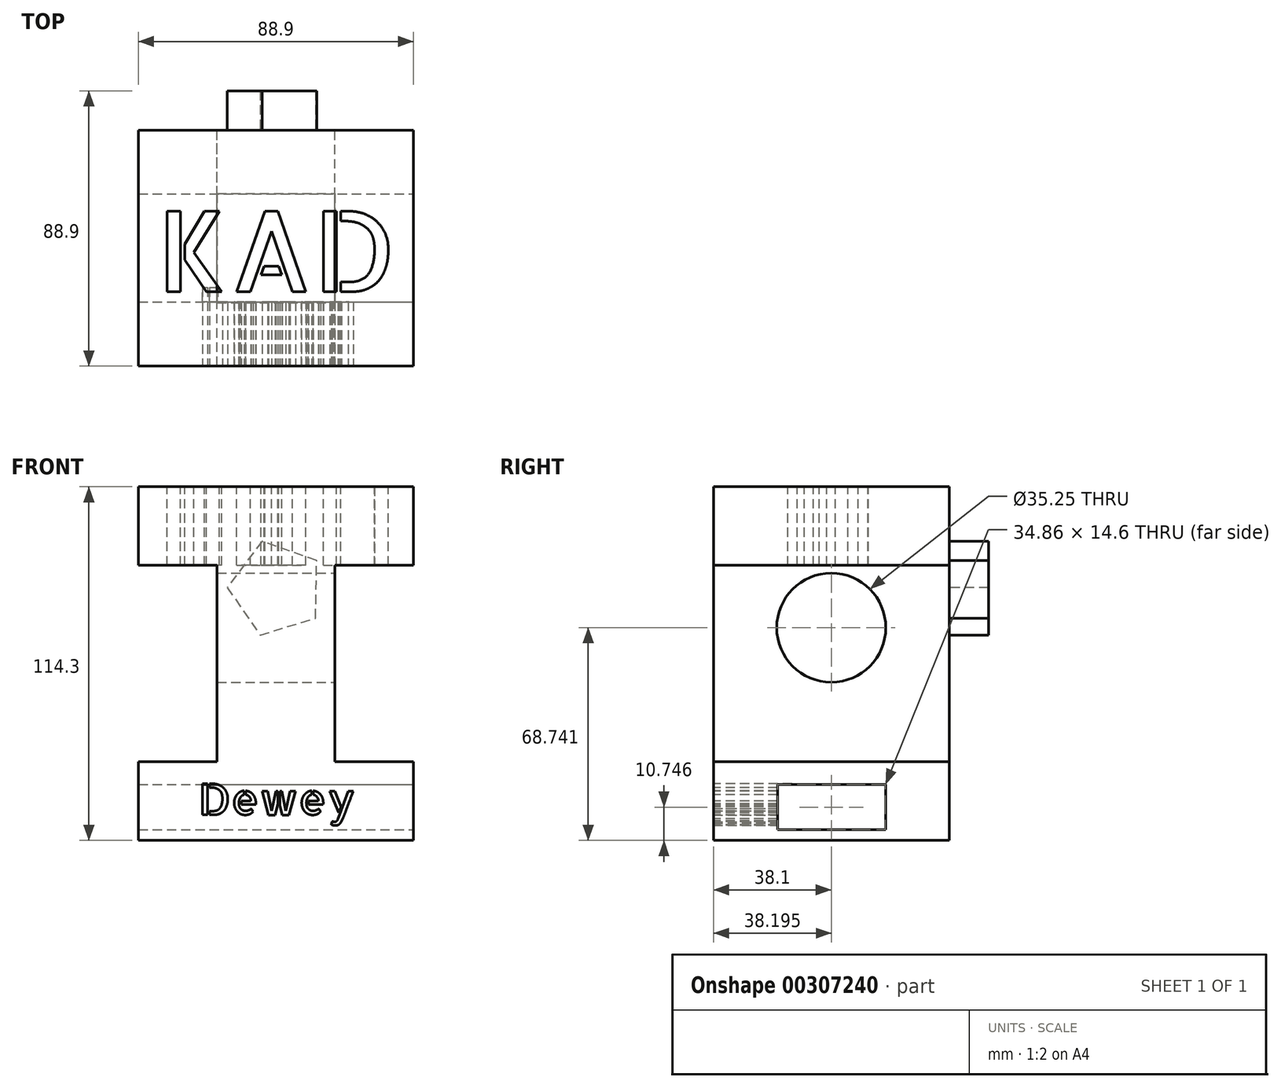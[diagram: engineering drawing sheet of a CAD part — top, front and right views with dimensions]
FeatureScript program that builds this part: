
annotation { "Feature Type Name" : "Feature", "Feature Type Description" : "" }
export const myFeature = defineFeature(function(context is Context, id is Id, definition is map)
    precondition{}
    {
        {
            var Q0;
            Q0=qCreatedBy(makeId("Front.planeOp"),FACE);
            var sketch = newSketch(context, id + "F0", { "sketchPlane" : qUnion([Q0])});
            skLineSegment(sketch, "E0", {"start": v(-31.57, -38.53) * mm, "end": v(57.33, -38.53) * mm});
            skLineSegment(sketch, "E1", {"start": v(57.33, -13.13) * mm, "end": v(57.33, -38.53) * mm});
            skLineSegment(sketch, "E2", {"start": v(57.33, -13.13) * mm, "end": v(31.93, -13.13) * mm});
            skLineSegment(sketch, "E3", {"start": v(31.93, -13.13) * mm, "end": v(31.93, 50.37) * mm});
            skLineSegment(sketch, "E4", {"start": v(31.93, 50.37) * mm, "end": v(57.33, 50.37) * mm});
            skLineSegment(sketch, "E5", {"start": v(57.33, 50.37) * mm, "end": v(57.33, 75.77) * mm});
            skLineSegment(sketch, "E6", {"start": v(57.33, 75.77) * mm, "end": v(-31.57, 75.77) * mm});
            skLineSegment(sketch, "E7", {"start": v(-31.57, 75.77) * mm, "end": v(-31.57, 50.37) * mm});
            skLineSegment(sketch, "E8", {"start": v(-31.57, 50.37) * mm, "end": v(-6.17, 50.37) * mm});
            skLineSegment(sketch, "E9", {"start": v(-6.17, 50.37) * mm, "end": v(-6.17, -13.13) * mm});
            skLineSegment(sketch, "E10", {"start": v(-6.17, -13.13) * mm, "end": v(-31.57, -13.13) * mm});
            skLineSegment(sketch, "E11", {"start": v(-31.57, -13.13) * mm, "end": v(-31.57, -38.53) * mm});
            skSolve(sketch);
        }
        {
            var Q0;
            Q0=makeQuery(id+"F0.imprint","IMPRINT",FACE,{"disambiguationData":[TD([[makeQuery(id+"F0.imprint","IMPRINT",EDGE,{"derivedFrom":sQuery(id+"F0.wireOp",EDGE,"E0")}),1.0]])]});
            extrude(context, id + "F1", {"entities" : qUnion([Q0]), "depth" : 76.2 * mm});
        }
        {
            var Q0;
            Q0=makeQuery(id+"F1.opExtrude","SWEPT_FACE",FACE,{"disambiguationData":[OSD([sQuery(id+"F0.wireOp",EDGE,"E3")])]});
            var sketch = newSketch(context, id + "F2", { "sketchPlane" : qUnion([Q0])});
            skCircle(sketch, "E12", {"center": v(-38.1, 30.21) * mm, "radius": 17.62 * mm});
            skPoint(sketch, "E12.centerSnap0", {"position": v(-38.1, 50.37) * mm});
            skSolve(sketch);
        }
        {
            var Q0;
            Q0=makeQuery(id+"F2.imprint","IMPRINT",FACE,{"disambiguationData":[TD([[makeQuery(id+"F2.imprint","IMPRINT",EDGE,{"derivedFrom":sQuery(id+"F2.wireOp",EDGE,"E12")}),1.0]])]});
            var Q1;
            Q1=sQuery(id+"F2.wireOp",EDGE,"E12");
            extrude(context, id + "F3", {"entities" : qUnion([Q0]), "operationType" : NewBodyOperationType.REMOVE, "surfaceEntities" : qUnion([Q1]), "endBound" : BoundingType.THROUGH_ALL, "oppositeDirection" : true, "depth" : 25.4 * mm});
        }
        {
            var Q0;
            Q0=makeQuery(id+"F1.opExtrude","SWEPT_FACE",FACE,{"disambiguationData":[OSD([sQuery(id+"F0.wireOp",EDGE,"E6")])]});
            var sketch = newSketch(context, id + "F4", { "sketchPlane" : qUnion([Q0])});
            skText(sketch, "E13", { "text": "KAD", "fontName": "AllertaStencil-Regular.ttf"});
            const initialGuessF4  = {"E13": [-0.0256, -0.05217, 1, 0, 0.02604]};
            skSetInitialGuess(sketch, initialGuessF4);
            skSolve(sketch);
        }
        {
            var Q0;
            Q0 = qSketchRegion(id + "F4", true);
            extrude(context, id + "F5", {"entities" : qUnion([Q0]), "operationType" : NewBodyOperationType.REMOVE, "oppositeDirection" : true, "depth" : 25.4 * mm});
        }
        {
            var Q0;
            Q0=makeQuery(id+"F1.opExtrude","SWEPT_FACE",FACE,{"disambiguationData":[OSD([sQuery(id+"F0.wireOp",EDGE,"E1")])]});
            var sketch = newSketch(context, id + "F6", { "sketchPlane" : qUnion([Q0])});
            skLineSegment(sketch, "E14.bottom", {"start": v(-20.57, -20.48) * mm, "end": v(-55.44, -20.48) * mm});
            skLineSegment(sketch, "E14.top", {"start": v(-20.57, -35.08) * mm, "end": v(-55.44, -35.08) * mm});
            skLineSegment(sketch, "E14.left", {"start": v(-20.57, -20.48) * mm, "end": v(-20.57, -35.08) * mm});
            skLineSegment(sketch, "E14.right", {"start": v(-55.44, -20.48) * mm, "end": v(-55.44, -35.08) * mm});
            skSolve(sketch);
        }
        {
            var Q0;
            Q0=makeQuery(id+"F6.imprint","IMPRINT",FACE,{"disambiguationData":[TD([[makeQuery(id+"F6.imprint","IMPRINT",EDGE,{"derivedFrom":sQuery(id+"F6.wireOp",EDGE,"E14.bottom")}),1.0]])]});
            extrude(context, id + "F7", {"entities" : qUnion([Q0]), "operationType" : NewBodyOperationType.REMOVE, "endBound" : BoundingType.THROUGH_ALL, "oppositeDirection" : true, "depth" : 25.4 * mm});
        }
        {
            var Q0;
            Q0=makeQuery(id+"F1.opExtrude","CAP_FACE",FACE,{"disambiguationData":[OSD([sQuery(id+"F0.wireOp",EDGE,"E0"),sQuery(id+"F0.wireOp",EDGE,"E1"),sQuery(id+"F0.wireOp",EDGE,"E2"),sQuery(id+"F0.wireOp",EDGE,"E3"),sQuery(id+"F0.wireOp",EDGE,"E4"),sQuery(id+"F0.wireOp",EDGE,"E5"),sQuery(id+"F0.wireOp",EDGE,"E6"),sQuery(id+"F0.wireOp",EDGE,"E7"),sQuery(id+"F0.wireOp",EDGE,"E8"),sQuery(id+"F0.wireOp",EDGE,"E9"),sQuery(id+"F0.wireOp",EDGE,"E10"),sQuery(id+"F0.wireOp",EDGE,"E11")])],"isStart":true});
            var sketch = newSketch(context, id + "F8", { "sketchPlane" : qUnion([Q0])});
            skCircle(sketch, "E15.cCircle", {"center": v(-13, 42.87) * mm, "radius": 15.9 * mm, "construction": true});
            skLineSegment(sketch, "E15.0", {"start": v(-25.69, 33.27) * mm, "end": v(-26.05, 51.97) * mm});
            skLineSegment(sketch, "E15.1", {"start": v(-26.05, 51.97) * mm, "end": v(-8.37, 58.09) * mm});
            skLineSegment(sketch, "E15.2", {"start": v(-8.37, 58.09) * mm, "end": v(2.9, 43.17) * mm});
            skLineSegment(sketch, "E15.3", {"start": v(2.9, 43.17) * mm, "end": v(-7.8, 27.83) * mm});
            skLineSegment(sketch, "E15.4", {"start": v(-7.8, 27.83) * mm, "end": v(-25.69, 33.27) * mm});
            skSolve(sketch);
        }
        {
            var Q0;
            Q0=makeQuery(id+"F8.imprint","IMPRINT",FACE,{"disambiguationData":[TD([[makeQuery(id+"F8.imprint","IMPRINT",EDGE,{"derivedFrom":sQuery(id+"F8.wireOp",EDGE,"E15.0")}),-1.0]])]});
            extrude(context, id + "F9", {"entities" : qUnion([Q0]), "operationType" : NewBodyOperationType.ADD, "depth" : 12.7 * mm});
        }
        {
            var Q0;
            Q0=makeQuery(id+"F1.opExtrude","CAP_FACE",FACE,{"disambiguationData":[OSD([sQuery(id+"F0.wireOp",EDGE,"E0"),sQuery(id+"F0.wireOp",EDGE,"E1"),sQuery(id+"F0.wireOp",EDGE,"E2"),sQuery(id+"F0.wireOp",EDGE,"E3"),sQuery(id+"F0.wireOp",EDGE,"E4"),sQuery(id+"F0.wireOp",EDGE,"E5"),sQuery(id+"F0.wireOp",EDGE,"E6"),sQuery(id+"F0.wireOp",EDGE,"E7"),sQuery(id+"F0.wireOp",EDGE,"E8"),sQuery(id+"F0.wireOp",EDGE,"E9"),sQuery(id+"F0.wireOp",EDGE,"E10"),sQuery(id+"F0.wireOp",EDGE,"E11")])],"isStart":false});
            var sketch = newSketch(context, id + "F10", { "sketchPlane" : qUnion([Q0])});
            skText(sketch, "E16", { "text": "Dewey", "fontName": "AllertaStencil-Regular.ttf"});
            const initialGuessF10  = {"E16": [-0.01215, -0.03029, 1, 0, 0.01008]};
            skSetInitialGuess(sketch, initialGuessF10);
            skSolve(sketch);
        }
        {
            var Q0;
            Q0 = qSketchRegion(id + "F10", true);
            extrude(context, id + "F11", {"entities" : qUnion([Q0]), "operationType" : NewBodyOperationType.REMOVE, "oppositeDirection" : true, "depth" : 25.4 * mm});
        }
    });
